# Revit family: MLR121LH_SET
name_source: partatom
category: Specialty Equipment
units: mm (PartAtom-declared; Revit-internal decimal feet)

## family parameters
Always vertical = Yes
Cut with Voids When Loaded = No
OmniClass Number = 23.40.20.21.47
OmniClass Title = Bath Grab Bars
Part Type = Normal
Room Calculation Point = No
Round Connector Dimension = Use Diameter
Shared = No
Work Plane-Based = No

## types (1)
- MLR120LH
    Description = 30° Flush Mount Wrap Around Grab Rail RH
    Manufacture_Depth = 1477 mm
    Manufacturer = Metlam
    Manufacturer_Height = 450 mm  [stored 1.47638 ft]
    Manufacturer_Spec Code = MLR114MKII
    Manufacturer_URL__Product Specific = https://www.metlam.com.au
    Manufacturer_Width = 1121 mm
    Material_ANZRS = z_Metlam_Metal_Stainless Steel_Satin
    Model = MLR114MKII
    PVC = PVC
    Type Comments = Grab Rails
    URL = http://www.metlam.com.au

note: [stored X ft] marks values corroborated as IEEE doubles in the binary element streams (Revit-internal decimal feet)

## geometry (parser evidence)
native form markers: Sweep x6
no freeform markers — native parametric forms only
